# Revit family: Verano_V870_Belluno_GM_R21_Wall Attached 2
name_source: partatom
category: Generic Models
units: mm (PartAtom-declared; Revit-internal decimal feet)

## family parameters
Always vertical = Yes
Can host rebar = No
Cut with Voids When Loaded = No
Part Type = Normal
Room Calculation Point = No
Round Connector Dimension = Use Diameter
Shared = No
Work Plane-Based = No

## types (3) — shared parameters
Manufacturer = Verano Systems
Model = V870 Belluno
zero-valued in all types: Default Elevation

## per-type parameters (varying)
| type | Freestanding - Double Parallel | Freestanding - Double Series | Freestanding-Single | Pillar 1 Visibility | Pillar 2 Visibility | Pillar 3 Visibility | TYPE | URL |
| TYPE 1 - Single | No | No | Yes | Yes | No | No | 1 |  |
| TYPE 2 - Double Parallel | Yes | No | No | No | Yes | No | 2 |  |
| TYPE 3 - Double Series | No | Yes | No | Yes | No | Yes | 3 | https://verano.nl |

## geometry (parser evidence)
native form markers: Sweep x18
no freeform markers — native parametric forms only
